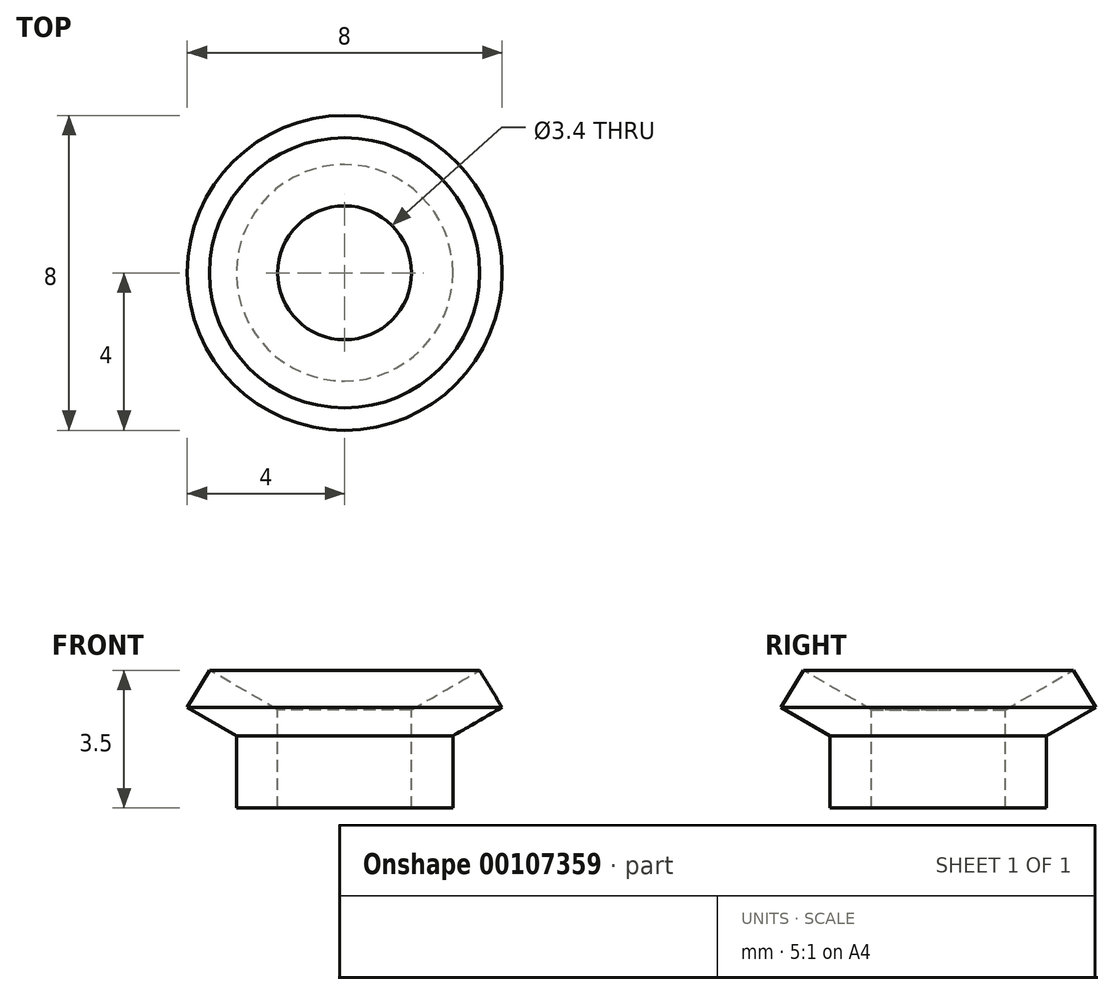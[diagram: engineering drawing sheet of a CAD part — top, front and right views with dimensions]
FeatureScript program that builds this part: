
annotation { "Feature Type Name" : "Feature", "Feature Type Description" : "" }
export const myFeature = defineFeature(function(context is Context, id is Id, definition is map)
    precondition{}
    {
        {
            var Q0;
            Q0=qCreatedBy(makeId("Right.planeOp"),FACE);
            var sketch = newSketch(context, id + "F0", { "sketchPlane" : qUnion([Q0])});
            skLineSegment(sketch, "E0", {"start": v(-1.7, 0) * mm, "end": v(-1.7, 2.5) * mm});
            skLineSegment(sketch, "E1", {"start": v(-1.7, 2.5) * mm, "end": v(-3.43, 3.5) * mm});
            skLineSegment(sketch, "E2", {"start": v(-3.43, 3.5) * mm, "end": v(-4, 2.56) * mm});
            skLineSegment(sketch, "E3", {"start": v(-4, 2.56) * mm, "end": v(-2.75, 1.84) * mm});
            skLineSegment(sketch, "E4", {"start": v(-2.75, 1.84) * mm, "end": v(-2.75, 0) * mm});
            skLineSegment(sketch, "E5", {"start": v(-2.75, 0) * mm, "end": v(-1.7, 0) * mm});
            skLineSegment(sketch, "E6", {"start": v(0, 3.37) * mm, "end": v(0, 0) * mm});
            skSolve(sketch);
        }
        {
            var Q0;
            Q0=qSketchRegion(id+"F0",true);
            var Q1;
            Q1=sQuery(id+"F0.wireOp",EDGE,"E6");
            revolve(context, id + "F1", {"entities" : qUnion([Q0]), "axis" : qUnion([Q1]), "revolveType" : RevolveType.FULL});
        }
    });
